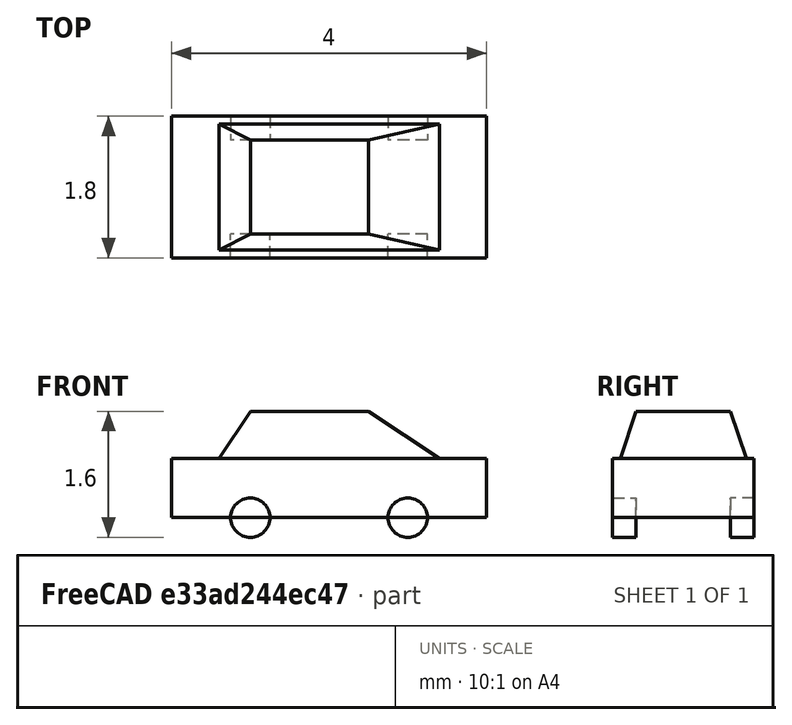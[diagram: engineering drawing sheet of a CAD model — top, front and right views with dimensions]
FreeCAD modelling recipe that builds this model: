
FCSTD DOCUMENT  (FreeCAD 0.18.4R)
Label: box
License: All rights reserved
LicenseURL: http://en.wikipedia.org/wiki/All_rights_reserved
objects: Part::Cylinder×4, Part::Box×1, Part::Wedge×1
note: 6 computed .brp shape members not serialized (recipe doc carries the construction recipe); baked Part::Feature solids carry a one-line shape summary decoded from their .brp

FEATURE [Part::Box] Box  label="bottom"
  AttacherType = Attacher::AttachEngine3D
  Height = 0.75
  Length = 4
  Placement = pos=(-2,-0.9,0.25) rot=(0,0,1;0rad)
  Width = 1.8
FEATURE [Part::Wedge] Wedge  label="top"
  AttacherType = Attacher::AttachEngine3D
  Placement = pos=(0,0,1) rot=(1,0,0;1.5708rad)
  X2max = 0.5
  X2min = -1
  Xmax = 1.4
  Xmin = -1.4
  Ymax = 0.6
  Ymin = 0
  Z2max = 0.6
  Z2min = -0.6
  Zmax = 0.8
  Zmin = -0.8
FEATURE [Part::Cylinder] Cylinder  label="front left"
  Angle = 360
  AttacherType = Attacher::AttachEngine3D
  Height = 0.3
  Placement = pos=(1,0.9,0.25) rot=(1,0,0;1.5708rad)
  Radius = 0.25
FEATURE [Part::Cylinder] Cylinder001  label="back left"
  Angle = 360
  AttacherType = Attacher::AttachEngine3D
  Height = 0.3
  Placement = pos=(-1,0.9,0.25) rot=(1,0,0;1.5708rad)
  Radius = 0.25
FEATURE [Part::Cylinder] Cylinder002  label="front right"
  Angle = 360
  AttacherType = Attacher::AttachEngine3D
  Height = 0.3
  Placement = pos=(1,-0.9,0.25) rot=(1,0,0;-1.5708rad)
  Radius = 0.25
FEATURE [Part::Cylinder] Cylinder003  label="back right"
  Angle = 360
  AttacherType = Attacher::AttachEngine3D
  Height = 0.3
  Placement = pos=(-1,-0.9,0.25) rot=(-1,0,0;1.5708rad)
  Radius = 0.25
